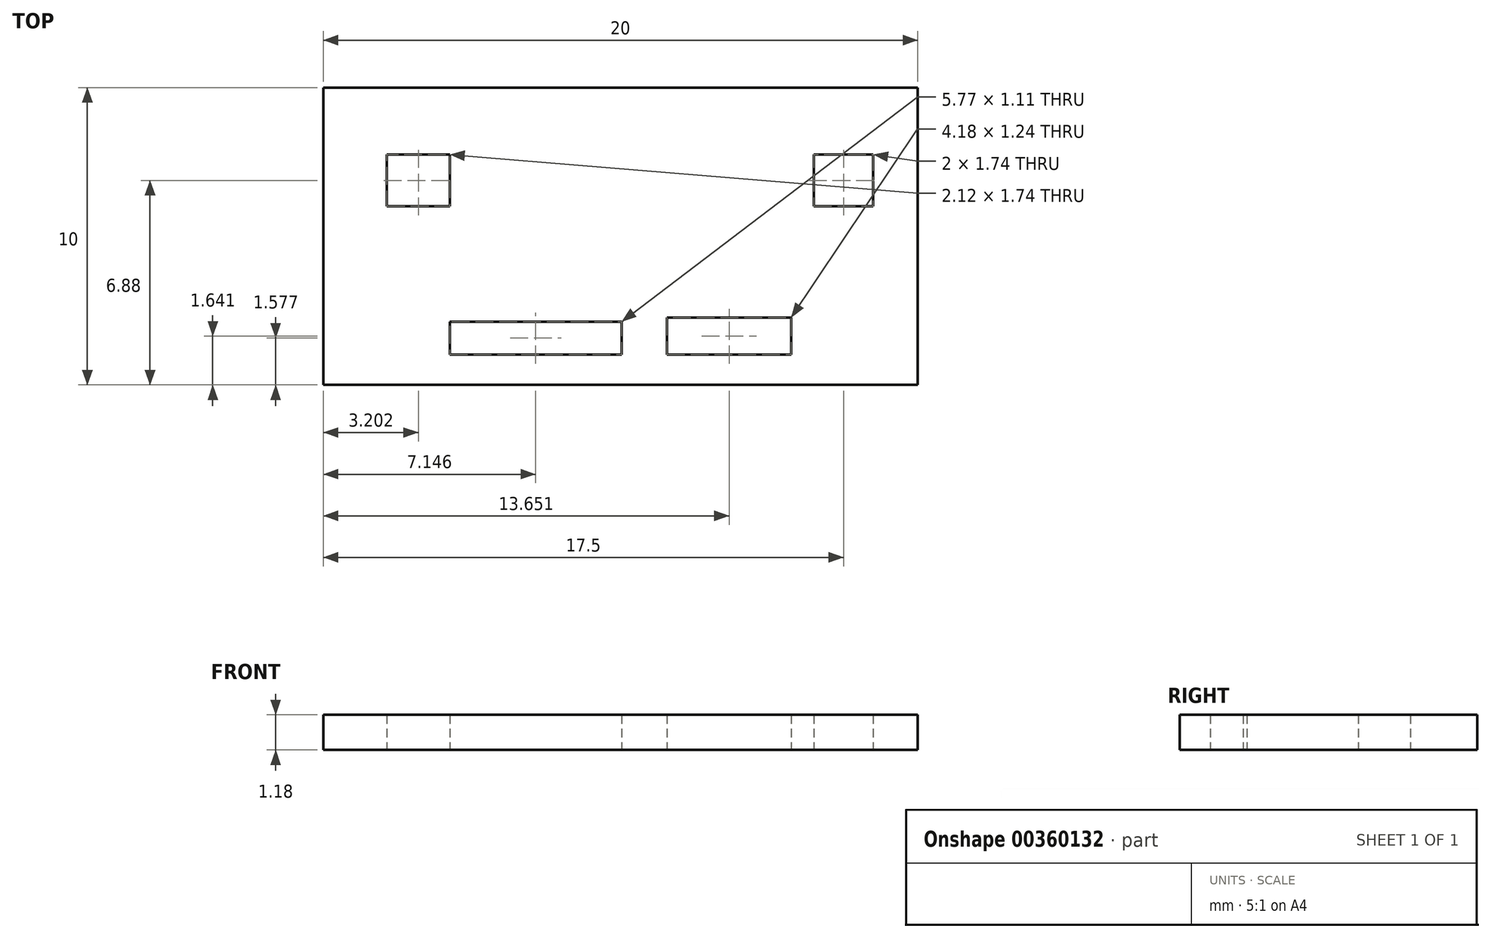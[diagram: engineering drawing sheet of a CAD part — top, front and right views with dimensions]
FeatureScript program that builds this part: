
annotation { "Feature Type Name" : "Feature", "Feature Type Description" : "" }
export const myFeature = defineFeature(function(context is Context, id is Id, definition is map)
    precondition{}
    {
        {
            var Q0;
            Q0=qCreatedBy(makeId("Top.planeOp"),FACE);
            var sketch = newSketch(context, id + "F0", { "sketchPlane" : qUnion([Q0])});
            skLineSegment(sketch, "E0.bottom", {"start": v(0, 0) * mm, "end": v(20, 0) * mm});
            skLineSegment(sketch, "E0.top", {"start": v(0, 10) * mm, "end": v(20, 10) * mm});
            skLineSegment(sketch, "E0.left", {"start": v(0, 0) * mm, "end": v(0, 10) * mm});
            skLineSegment(sketch, "E0.right", {"start": v(20, 0) * mm, "end": v(20, 10) * mm});
            skLineSegment(sketch, "E1.bottom", {"start": v(4.26, 2.13) * mm, "end": v(10.03, 2.13) * mm});
            skLineSegment(sketch, "E1.top", {"start": v(4.26, 1.02) * mm, "end": v(10.03, 1.02) * mm});
            skLineSegment(sketch, "E1.left", {"start": v(4.26, 2.13) * mm, "end": v(4.26, 1.02) * mm});
            skLineSegment(sketch, "E1.right", {"start": v(10.03, 2.13) * mm, "end": v(10.03, 1.02) * mm});
            skLineSegment(sketch, "E2.bottom", {"start": v(11.56, 2.26) * mm, "end": v(15.74, 2.26) * mm});
            skLineSegment(sketch, "E2.top", {"start": v(11.56, 1.02) * mm, "end": v(15.74, 1.02) * mm});
            skLineSegment(sketch, "E2.left", {"start": v(11.56, 2.26) * mm, "end": v(11.56, 1.02) * mm});
            skLineSegment(sketch, "E2.right", {"start": v(15.74, 2.26) * mm, "end": v(15.74, 1.02) * mm});
            skLineSegment(sketch, "E3.bottom", {"start": v(16.5, 7.75) * mm, "end": v(18.5, 7.75) * mm});
            skLineSegment(sketch, "E3.top", {"start": v(16.5, 6) * mm, "end": v(18.5, 6) * mm});
            skLineSegment(sketch, "E3.left", {"start": v(16.5, 7.75) * mm, "end": v(16.5, 6) * mm});
            skLineSegment(sketch, "E3.right", {"start": v(18.5, 7.75) * mm, "end": v(18.5, 6) * mm});
            skLineSegment(sketch, "E4.bottom", {"start": v(4.26, 7.75) * mm, "end": v(2.14, 7.75) * mm});
            skLineSegment(sketch, "E4.top", {"start": v(4.26, 6) * mm, "end": v(2.14, 6) * mm});
            skLineSegment(sketch, "E4.left", {"start": v(4.26, 7.75) * mm, "end": v(4.26, 6) * mm});
            skLineSegment(sketch, "E4.right", {"start": v(2.14, 7.75) * mm, "end": v(2.14, 6) * mm});
            skSolve(sketch);
        }
        {
            var Q0;
            Q0=makeQuery(id+"F0.imprint","IMPRINT",FACE,{"disambiguationData":[TD([[makeQuery(id+"F0.imprint","IMPRINT",EDGE,{"derivedFrom":sQuery(id+"F0.wireOp",EDGE,"E0.bottom")}),1.0]])]});
            extrude(context, id + "F1", {"entities" : qUnion([Q0]), "depth" : 1.18 * mm});
        }
    });
